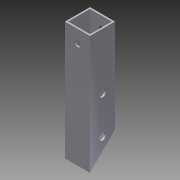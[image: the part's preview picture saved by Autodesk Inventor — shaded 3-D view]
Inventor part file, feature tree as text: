
AUTODESK INVENTOR PART (.ipt)
format: ipt  version: 2014 SP1 (Build 180222100, 222)  size: 104,448 bytes
history: native  units: in
note: dims shown in document units (in); Inventor stores cm internally (conversion verified against a paired STEP export)
features: extrude x4, sketch x4, reference x4
ambient origin geometry x8: Origin, YZ Plane, XZ Plane, XY Plane, X Axis, Y Axis, Z Axis, Center Point
bodies: Solid1 (feature_tree)
feature tree (12):
  extrude  "Extrusion1"  Depth=1.0in
  extrude  "Extrusion2"  Depth=0.0625in TaperAngle=0.0deg
  extrude  "Extrusion3"  Depth=1.0in TaperAngle=0.0deg
  extrude  "Extrusion4"  Depth=1.0in TaperAngle=0.0deg
  sketch  "Sketch1"  dims[d0=1.0in d2=1.0in]
  sketch  "Sketch2"  dims[d3=0.0625in d4=4.75in d5=0.0in]
  sketch  "Sketch3"  dims[d6=45.0deg d7=1.0in d8=0.0in]
  reference  "Reference1"
  reference  "Reference2"
  sketch  "Sketch4"  dims[d9=1.0in d10=0.0in d11=1.0in d12=0.0in]
  reference  "Reference3"
  reference  "Reference4"
